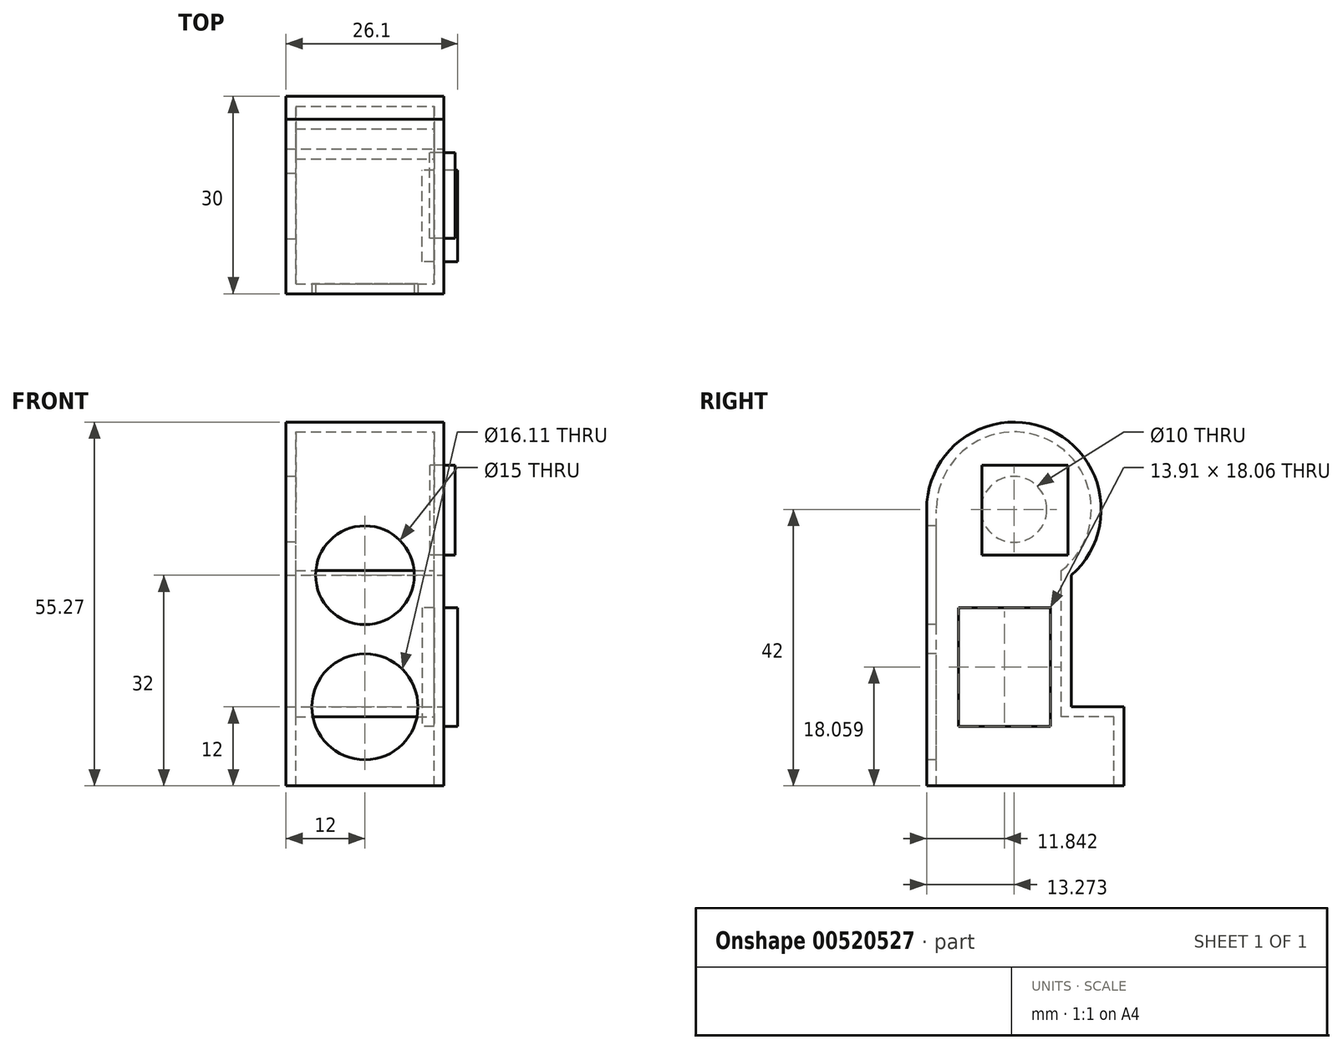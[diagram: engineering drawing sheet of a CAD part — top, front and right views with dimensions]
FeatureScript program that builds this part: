
annotation { "Feature Type Name" : "Feature", "Feature Type Description" : "" }
export const myFeature = defineFeature(function(context is Context, id is Id, definition is map)
    precondition{}
    {
        {
            var Q0;
            Q0=qCreatedBy(makeId("Right.planeOp"),FACE);
            var sketch = newSketch(context, id + "F0", { "sketchPlane" : qUnion([Q0])});
            skLineSegment(sketch, "E0", {"start": v(0, 0) * mm, "end": v(0, 42) * mm});
            skLineSegment(sketch, "E1", {"start": v(0, 0) * mm, "end": v(30, 0) * mm});
            skLineSegment(sketch, "E2", {"start": v(30, 0) * mm, "end": v(30, 12) * mm});
            skLineSegment(sketch, "E3", {"start": v(30, 12) * mm, "end": v(22, 12) * mm});
            skLineSegment(sketch, "E4", {"start": v(22, 12) * mm, "end": v(22, 32) * mm});
            skArc(sketch, "E5", {"start": v(22, 32) * mm, "mid": v(18.77, 54.08) * mm, "end": v(0, 42) * mm});
            skSolve(sketch);
        }
        {
            var Q0;
            Q0=makeQuery(id+"F0.imprint","IMPRINT",FACE,{"disambiguationData":[TD([[makeQuery(id+"F0.imprint","IMPRINT",EDGE,{"derivedFrom":sQuery(id+"F0.wireOp",EDGE,"E0")}),-1.0]])]});
            extrude(context, id + "F1", {"entities" : qUnion([Q0]), "endBound" : BoundingType.SYMMETRIC, "depth" : 24 * mm});
        }
        {
            var Q0;
            Q0=makeQuery(id+"F1.opExtrude","SWEPT_FACE",FACE,{"disambiguationData":[OSD([sQuery(id+"F0.wireOp",EDGE,"E1")])]});
            shell(context, id + "F2", {"entities" : qUnion([Q0]), "thickness" : 1.5 * mm});
        }
        {
            var Q0;
            Q0=makeQuery(id+"F1.opExtrude","CAP_FACE",FACE,{"disambiguationData":[OSD([sQuery(id+"F0.wireOp",EDGE,"E0"),sQuery(id+"F0.wireOp",EDGE,"E1"),sQuery(id+"F0.wireOp",EDGE,"E2"),sQuery(id+"F0.wireOp",EDGE,"E3"),sQuery(id+"F0.wireOp",EDGE,"E4"),sQuery(id+"F0.wireOp",EDGE,"E5")])],"isStart":false});
            var sketch = newSketch(context, id + "F3", { "sketchPlane" : qUnion([Q0])});
            skCircle(sketch, "E6", {"center": v(13.27, 42) * mm, "radius": 5 * mm});
            skSolve(sketch);
        }
        {
            var Q0;
            Q0=qSketchRegion(id+"F3",true);
            extrude(context, id + "F4", {"entities" : qUnion([Q0]), "operationType" : NewBodyOperationType.REMOVE, "oppositeDirection" : true, "depth" : 5 * mm});
        }
        {
            var Q0;
            Q0=makeQuery(id+"F1.opExtrude","SWEPT_FACE",FACE,{"disambiguationData":[OSD([sQuery(id+"F0.wireOp",EDGE,"E0")])]});
            var sketch = newSketch(context, id + "F5", { "sketchPlane" : qUnion([Q0])});
            skCircle(sketch, "E7", {"center": v(0, 12) * mm, "radius": 8.05 * mm});
            skCircle(sketch, "E8", {"center": v(0, 32) * mm, "radius": 7.5 * mm});
            skSolve(sketch);
        }
        {
            var Q0;
            Q0=makeQuery(id+"F5.imprint","IMPRINT",FACE,{"disambiguationData":[TD([[makeQuery(id+"F5.imprint","IMPRINT",EDGE,{"derivedFrom":sQuery(id+"F5.wireOp",EDGE,"E8")}),1.0]])]});
            var Q1;
            Q1=makeQuery(id+"F5.imprint","IMPRINT",FACE,{"disambiguationData":[TD([[makeQuery(id+"F5.imprint","IMPRINT",EDGE,{"derivedFrom":sQuery(id+"F5.wireOp",EDGE,"E7")}),1.0]])]});
            extrude(context, id + "F6", {"entities" : qUnion([Q0, Q1]), "operationType" : NewBodyOperationType.REMOVE, "oppositeDirection" : true, "depth" : 5 * mm});
        }
        {
            var Q0;
            Q0=makeQuery(id+"F1.opExtrude","SWEPT_BODY",BODY,{"disambiguationData":[OSD([sQuery(id+"F0.wireOp",EDGE,"E0"),sQuery(id+"F0.wireOp",EDGE,"E1"),sQuery(id+"F0.wireOp",EDGE,"E2"),sQuery(id+"F0.wireOp",EDGE,"E3"),sQuery(id+"F0.wireOp",EDGE,"E4"),sQuery(id+"F0.wireOp",EDGE,"E5")])]});
            var Q1;
            Q1=makeQuery(id+"F1.opExtrude","CAP_FACE",FACE,{"disambiguationData":[OSD([sQuery(id+"F0.wireOp",EDGE,"E0"),sQuery(id+"F0.wireOp",EDGE,"E1"),sQuery(id+"F0.wireOp",EDGE,"E2"),sQuery(id+"F0.wireOp",EDGE,"E3"),sQuery(id+"F0.wireOp",EDGE,"E4"),sQuery(id+"F0.wireOp",EDGE,"E5")])],"isStart":false});
            mirror(context, id + "F7", {"entities" : qUnion([Q0]), "mirrorPlane" : qUnion([Q1])});
        }
        {
            var Q0;
            Q0=makeQuery(id+"F1.opExtrude","SWEPT_BODY",BODY,{"disambiguationData":[OSD([sQuery(id+"F0.wireOp",EDGE,"E0"),sQuery(id+"F0.wireOp",EDGE,"E1"),sQuery(id+"F0.wireOp",EDGE,"E2"),sQuery(id+"F0.wireOp",EDGE,"E3"),sQuery(id+"F0.wireOp",EDGE,"E4"),sQuery(id+"F0.wireOp",EDGE,"E5")])]});
            deleteBodies(context, id + "F8", {"entities" : qUnion([Q0])});
        }
        {
            var Q0;
            Q0=qCreatedBy(makeId("Right.planeOp"),FACE);
            var sketch = newSketch(context, id + "F9", { "sketchPlane" : qUnion([Q0])});
            skLineSegment(sketch, "E9.bottom", {"start": v(8.44, 48.7) * mm, "end": v(21.46, 48.7) * mm});
            skLineSegment(sketch, "E9.top", {"start": v(8.44, 35.08) * mm, "end": v(21.46, 35.08) * mm});
            skLineSegment(sketch, "E9.left", {"start": v(8.44, 48.7) * mm, "end": v(8.44, 35.08) * mm});
            skLineSegment(sketch, "E9.right", {"start": v(21.46, 48.7) * mm, "end": v(21.46, 35.08) * mm});
            skSolve(sketch);
        }
        {
            var Q0;
            Q0 = qSketchRegion(id + "F9", true);
            extrude(context, id + "F10", {"entities" : qUnion([Q0]), "depth" : 37.7 * mm, "offsetDistance" : 25 * mm, "hasSecondDirection" : true, "secondDirectionOppositeDirection" : false, "secondDirectionDepth" : 33.8 * mm});
        }
        {
            var Q0;
            Q0=qCreatedBy(makeId("Right.planeOp"),FACE);
            var sketch = newSketch(context, id + "F11", { "sketchPlane" : qUnion([Q0])});
            skLineSegment(sketch, "E10.bottom", {"start": v(4.88, 27.09) * mm, "end": v(18.8, 27.09) * mm});
            skLineSegment(sketch, "E10.top", {"start": v(4.88, 9.03) * mm, "end": v(18.8, 9.03) * mm});
            skLineSegment(sketch, "E10.left", {"start": v(4.88, 27.09) * mm, "end": v(4.88, 9.03) * mm});
            skLineSegment(sketch, "E10.right", {"start": v(18.8, 27.09) * mm, "end": v(18.8, 9.03) * mm});
            skSolve(sketch);
        }
        {
            var Q0;
            Q0 = qSketchRegion(id + "F11", true);
            extrude(context, id + "F12", {"entities" : qUnion([Q0]), "operationType" : NewBodyOperationType.ADD, "depth" : 38.1 * mm, "offsetDistance" : 25 * mm, "hasSecondDirection" : true, "secondDirectionOppositeDirection" : false, "secondDirectionDepth" : 32.7 * mm});
        }
    });
